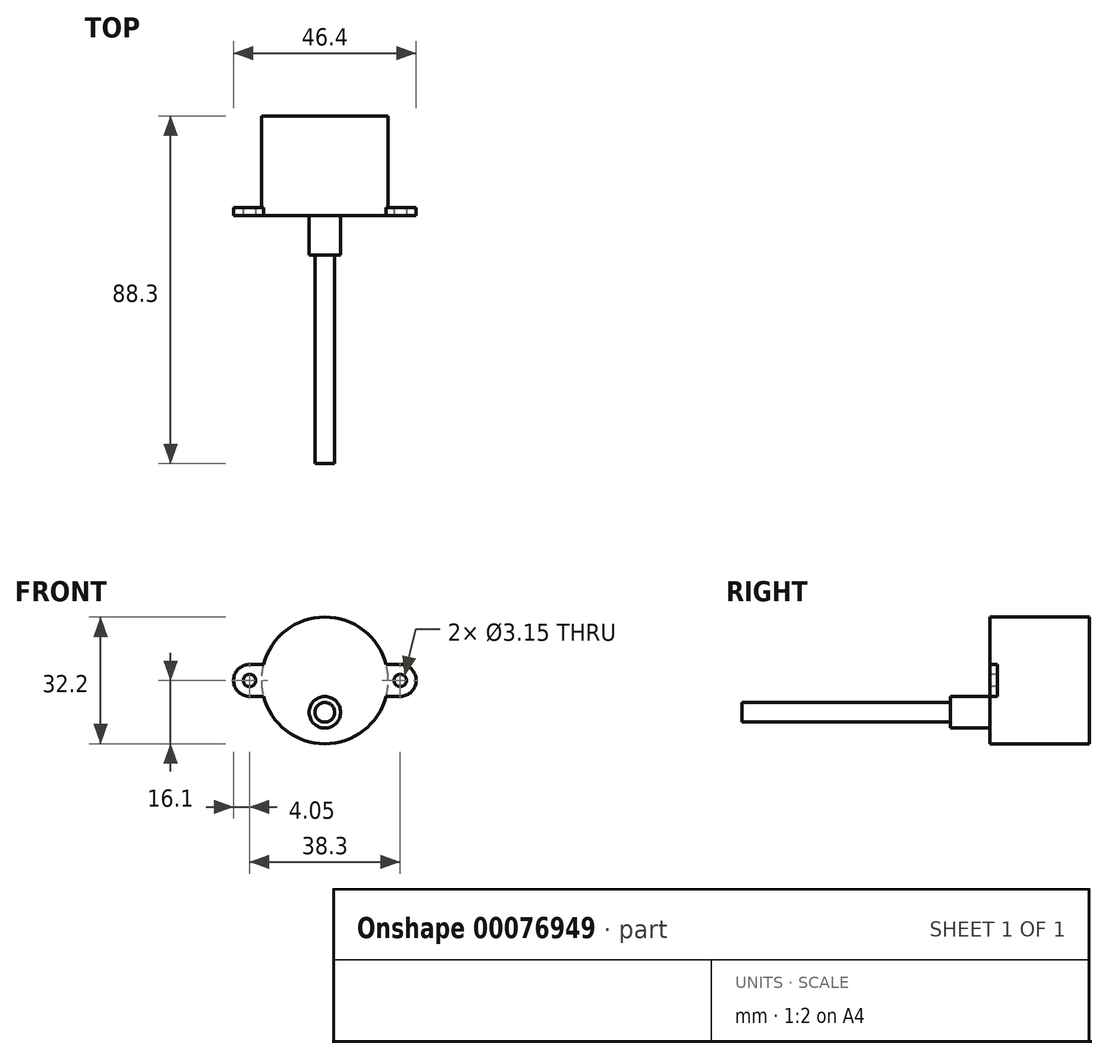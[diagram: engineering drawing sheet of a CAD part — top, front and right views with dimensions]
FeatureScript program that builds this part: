
annotation { "Feature Type Name" : "Feature", "Feature Type Description" : "" }
export const myFeature = defineFeature(function(context is Context, id is Id, definition is map)
    precondition{}
    {
        {
            var Q0;
            Q0=qCreatedBy(makeId("Front.planeOp"),FACE);
            var sketch = newSketch(context, id + "F0", { "sketchPlane" : qUnion([Q0])});
            skCircle(sketch, "E0", {"center": v(0, 8.1) * mm, "radius": 16.1 * mm});
            skCircle(sketch, "E1", {"center": v(0, 0) * mm, "radius": 2.5 * mm});
            skLineSegment(sketch, "E2", {"start": v(15.58, 12.15) * mm, "end": v(19.15, 12.15) * mm});
            skLineSegment(sketch, "E3", {"start": v(15.58, 4.05) * mm, "end": v(19.15, 4.05) * mm});
            skArc(sketch, "E4", {"start": v(19.15, 4.05) * mm, "mid": v(23.2, 8.1) * mm, "end": v(19.15, 12.15) * mm});
            skLineSegment(sketch, "E5", {"start": v(0, 8.1) * mm, "end": v(51.34, 8.1) * mm, "construction": true});
            skCircle(sketch, "E6", {"center": v(19.15, 8.1) * mm, "radius": 1.57 * mm});
            skLineSegment(sketch, "E7", {"start": v(0, 27.62) * mm, "end": v(0, 0) * mm, "construction": true});
            skLineSegment(sketch, "E8.MirrorCS", {"start": v(-15.58, 12.15) * mm, "end": v(-19.15, 12.15) * mm});
            skArc(sketch, "E9.MirrorCS", {"start": v(-19.15, 4.05) * mm, "mid": v(-23.2, 8.1) * mm, "end": v(-19.15, 12.15) * mm});
            skLineSegment(sketch, "E10.MirrorCS", {"start": v(-15.58, 4.05) * mm, "end": v(-19.15, 4.05) * mm});
            skCircle(sketch, "E11.MirrorC", {"center": v(-19.15, 8.1) * mm, "radius": 1.57 * mm});
            skSolve(sketch);
        }
        {
            var Q0;
            Q0=qCreatedBy(makeId("Front.planeOp"),FACE);
            var sketch = newSketch(context, id + "F1", { "sketchPlane" : qUnion([Q0])});
            skCircle(sketch, "E12.0", {"center": v(0, 8.1) * mm, "radius": 16.1 * mm});
            skSolve(sketch);
        }
        {
            var Q0;
            Q0=qSketchRegion(id+"F1",true);
            extrude(context, id + "F2", {"entities" : qUnion([Q0]), "oppositeDirection" : true, "depth" : 25.3 * mm});
        }
        {
            var Q0;
            Q0=qCreatedBy(makeId("Front.planeOp"),FACE);
            var sketch = newSketch(context, id + "F3", { "sketchPlane" : qUnion([Q0])});
            skArc(sketch, "E13.0", {"start": v(-19.15, 4.05) * mm, "mid": v(-23.2, 8.1) * mm, "end": v(-19.15, 12.15) * mm});
            skLineSegment(sketch, "E14.0", {"start": v(-15.58, 4.05) * mm, "end": v(-19.15, 4.05) * mm});
            skCircle(sketch, "E15.0", {"center": v(-19.15, 8.1) * mm, "radius": 1.57 * mm});
            skLineSegment(sketch, "E16.0", {"start": v(-15.58, 12.15) * mm, "end": v(-19.15, 12.15) * mm});
            skLineSegment(sketch, "E17.0", {"start": v(15.58, 12.15) * mm, "end": v(19.15, 12.15) * mm});
            skArc(sketch, "E18.0", {"start": v(19.15, 4.05) * mm, "mid": v(23.2, 8.1) * mm, "end": v(19.15, 12.15) * mm});
            skLineSegment(sketch, "E19.0", {"start": v(15.58, 4.05) * mm, "end": v(19.15, 4.05) * mm});
            skArc(sketch, "E20", {"start": v(-15.58, 12.15) * mm, "mid": v(-16.1, 8.1) * mm, "end": v(-15.58, 4.05) * mm});
            skArc(sketch, "E21", {"start": v(15.58, 4.05) * mm, "mid": v(16.1, 8.1) * mm, "end": v(15.58, 12.15) * mm});
            skCircle(sketch, "E22.0", {"center": v(19.15, 8.1) * mm, "radius": 1.57 * mm});
            skSolve(sketch);
        }
        {
            var Q0;
            Q0=qSketchRegion(id+"F3",true);
            extrude(context, id + "F4", {"entities" : qUnion([Q0]), "operationType" : NewBodyOperationType.ADD, "oppositeDirection" : true, "depth" : 2 * mm});
        }
        {
            var Q0;
            Q0=qCreatedBy(makeId("Front.planeOp"),FACE);
            var sketch = newSketch(context, id + "F5", { "sketchPlane" : qUnion([Q0])});
            skCircle(sketch, "E23.0", {"center": v(0, 0) * mm, "radius": 2.5 * mm});
            skSolve(sketch);
        }
        {
            var Q0;
            Q0=qSketchRegion(id+"F5",true);
            extrude(context, id + "F6", {"entities" : qUnion([Q0]), "operationType" : NewBodyOperationType.ADD, "depth" : 63 * mm});
        }
        {
            var Q0;
            Q0=makeQuery(id+"F0.imprint","IMPRINT",FACE,{"disambiguationData":[TD([[makeQuery(id+"F0.imprint","IMPRINT",EDGE,{"derivedFrom":sQuery(id+"F0.wireOp",EDGE,"E1")}),-1.0]])]});
            var sketch = newSketch(context, id + "F7", { "sketchPlane" : qUnion([Q0])});
            skCircle(sketch, "E24", {"center": v(0, 0) * mm, "radius": 4 * mm});
            skSolve(sketch);
        }
        {
            var Q0;
            Q0=qSketchRegion(id+"F7",true);
            extrude(context, id + "F8", {"entities" : qUnion([Q0]), "operationType" : NewBodyOperationType.ADD, "depth" : 10 * mm});
        }
    });
